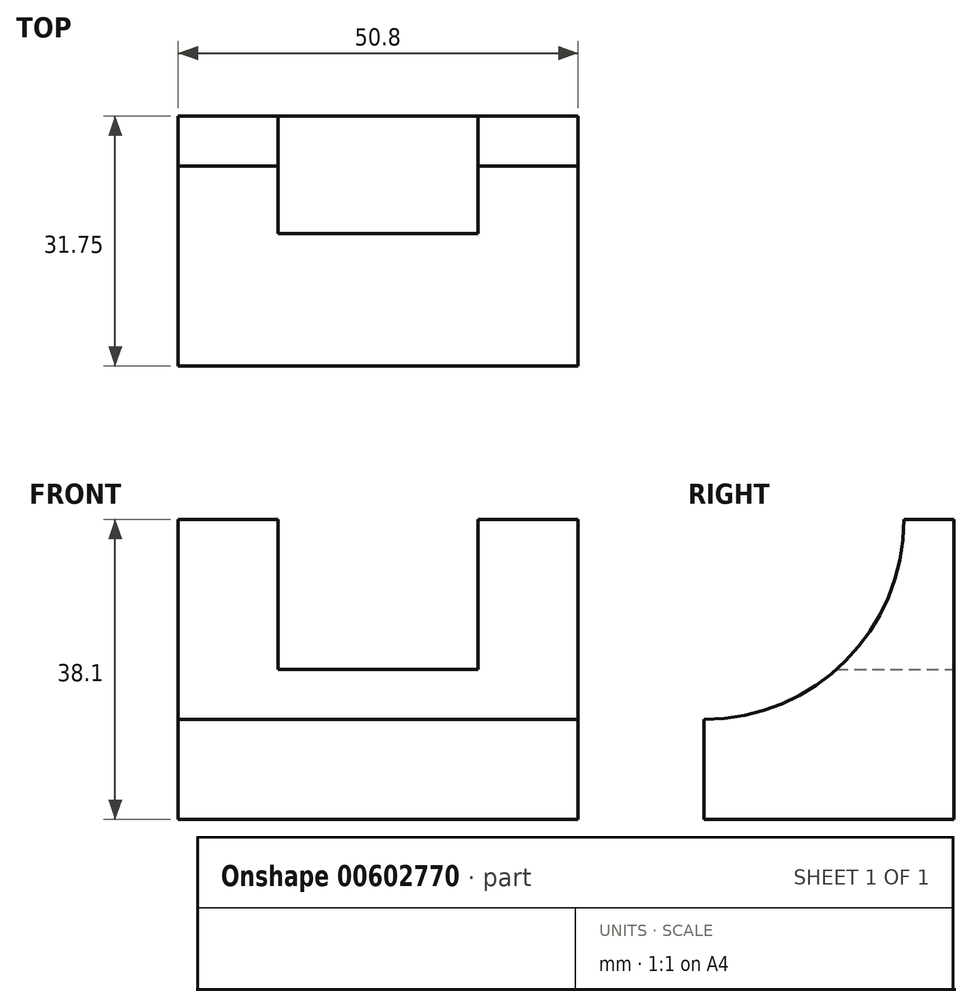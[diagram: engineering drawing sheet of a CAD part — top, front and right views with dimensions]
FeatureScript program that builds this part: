
annotation { "Feature Type Name" : "Feature", "Feature Type Description" : "" }
export const myFeature = defineFeature(function(context is Context, id is Id, definition is map)
    precondition{}
    {
        {
            var Q0;
            Q0=qCreatedBy(makeId("Front.planeOp"),FACE);
            var sketch = newSketch(context, id + "F0", { "sketchPlane" : qUnion([Q0])});
            skLineSegment(sketch, "E0", {"start": v(0, 0) * mm, "end": v(50.8, 0) * mm});
            skLineSegment(sketch, "E1", {"start": v(50.8, 0) * mm, "end": v(50.8, 38.1) * mm});
            skLineSegment(sketch, "E2", {"start": v(50.8, 38.1) * mm, "end": v(0, 38.1) * mm});
            skLineSegment(sketch, "E3", {"start": v(0, 38.1) * mm, "end": v(0, 0) * mm});
            skSolve(sketch);
        }
        {
            var Q0;
            Q0 = qSketchRegion(id + "F0", true);
            extrude(context, id + "F1", {"entities" : qUnion([Q0]), "depth" : 31.75 * mm, "offsetDistance" : 25.4 * mm});
        }
        {
            var Q0;
            Q0=makeQuery(id+"F1.opExtrude","SWEPT_FACE",FACE,{"disambiguationData":[OSD([sQuery(id+"F0.wireOp",EDGE,"E1")])]});
            var sketch = newSketch(context, id + "F2", { "sketchPlane" : qUnion([Q0])});
            skLineSegment(sketch, "E4.0.0", {"start": v(0, 0) * mm, "end": v(0, 38.1) * mm});
            skLineSegment(sketch, "E4.0.1", {"start": v(0, 38.1) * mm, "end": v(-31.75, 38.1) * mm});
            skLineSegment(sketch, "E4.0.2", {"start": v(-31.75, 38.1) * mm, "end": v(-31.75, 0) * mm});
            skLineSegment(sketch, "E4.0.3", {"start": v(-31.75, 0) * mm, "end": v(0, 0) * mm});
            skArc(sketch, "E5", {"start": v(-31.75, 12.7) * mm, "mid": v(-13.79, 20.14) * mm, "end": v(-6.35, 38.1) * mm});
            skSolve(sketch);
        }
        {
            var Q0;
            {var subQ3=sQuery(id+"F2.wireOp",EDGE,"E5");Q0=makeQuery(id+"F2.imprint","IMPRINT",FACE,{"disambiguationData":[TD([[makeQuery(id+"F2.imprint","IMPRINT",EDGE,{"derivedFrom":subQ3}),1.0]])]});}
            extrude(context, id + "F3", {"entities" : qUnion([Q0]), "operationType" : NewBodyOperationType.REMOVE, "oppositeDirection" : true, "depth" : 50.8 * mm, "offsetDistance" : 25.4 * mm});
        }
        {
            var Q0;
            Q0=makeQuery(id+"F1.opExtrude","CAP_FACE",FACE,{"disambiguationData":[OSD([sQuery(id+"F0.wireOp",EDGE,"E0"),sQuery(id+"F0.wireOp",EDGE,"E1"),sQuery(id+"F0.wireOp",EDGE,"E2"),sQuery(id+"F0.wireOp",EDGE,"E3")])],"isStart":true});
            var sketch = newSketch(context, id + "F4", { "sketchPlane" : qUnion([Q0])});
            skLineSegment(sketch, "E6", {"start": v(-38.1, 38.1) * mm, "end": v(-38.1, 19.05) * mm});
            skLineSegment(sketch, "E7", {"start": v(-38.1, 19.05) * mm, "end": v(-12.7, 19.05) * mm});
            skLineSegment(sketch, "E8", {"start": v(-12.7, 19.05) * mm, "end": v(-12.7, 38.1) * mm});
            skSolve(sketch);
        }
        {
            var Q0;
            {var subQ0=sQuery(id+"F4.wireOp",EDGE,"E6");Q0=makeQuery(id+"F4.imprint","IMPRINT",FACE,{"disambiguationData":[TD([[makeQuery(id+"F4.imprint","IMPRINT",EDGE,{"derivedFrom":subQ0}),1.0]])]});}
            extrude(context, id + "F5", {"entities" : qUnion([Q0]), "operationType" : NewBodyOperationType.REMOVE, "oppositeDirection" : true, "depth" : 51.43 * mm, "offsetDistance" : 25.4 * mm});
        }
    });
